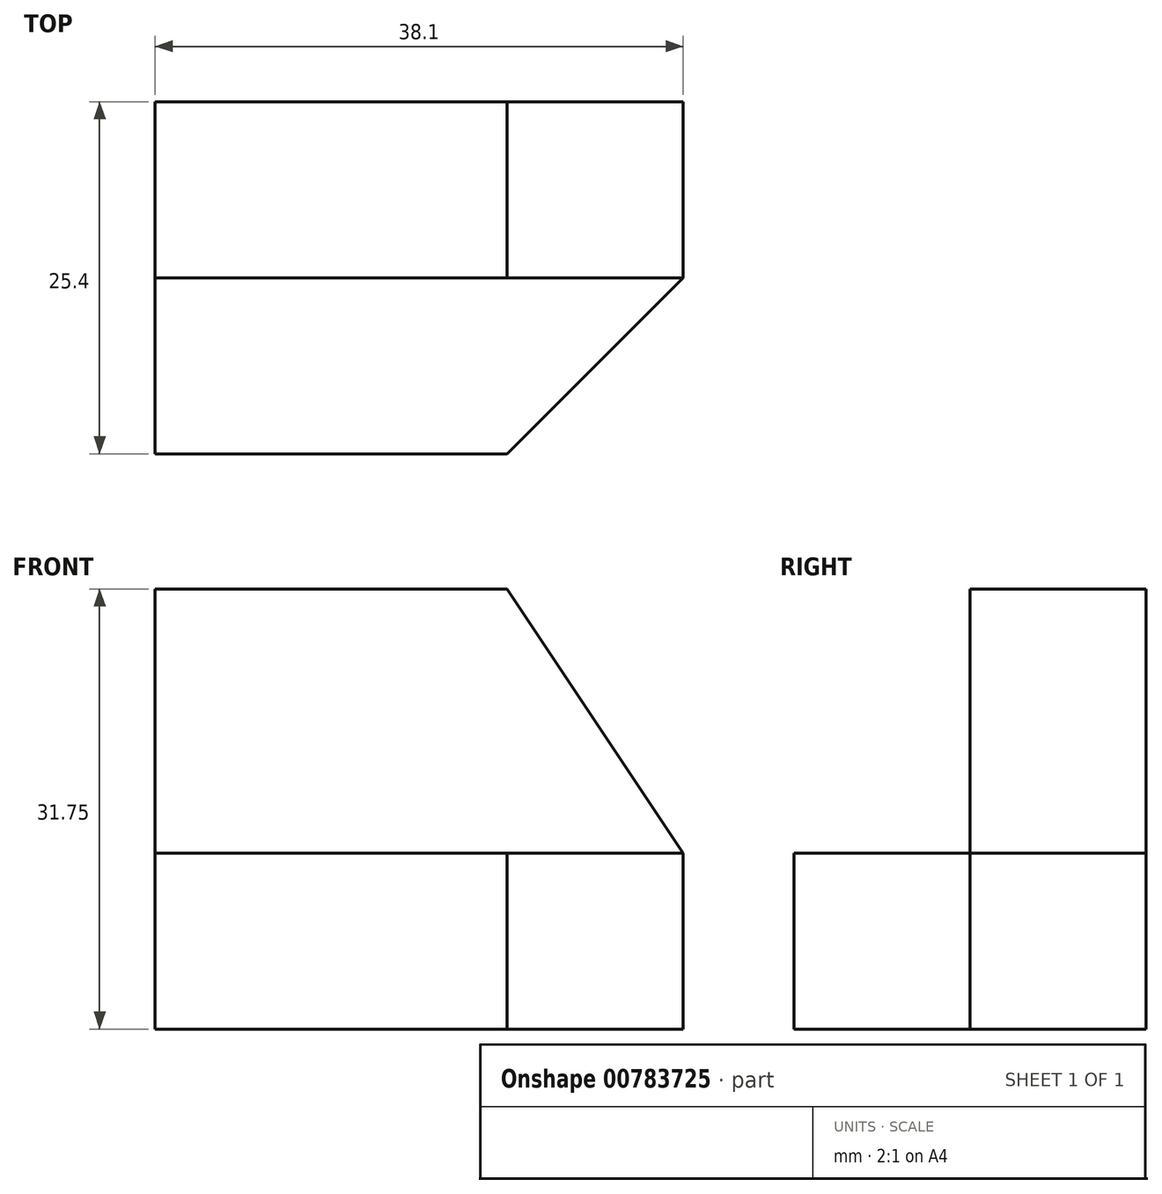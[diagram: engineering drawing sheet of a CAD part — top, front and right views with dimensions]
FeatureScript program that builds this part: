
annotation { "Feature Type Name" : "Feature", "Feature Type Description" : "" }
export const myFeature = defineFeature(function(context is Context, id is Id, definition is map)
    precondition{}
    {
        {
            var Q0;
            Q0=qCreatedBy(makeId("Front.planeOp"),FACE);
            var sketch = newSketch(context, id + "F0", { "sketchPlane" : qUnion([Q0])});
            skLineSegment(sketch, "E0", {"start": v(0, 0) * mm, "end": v(38.1, 0) * mm});
            skLineSegment(sketch, "E1", {"start": v(0, 0) * mm, "end": v(0, 31.75) * mm});
            skLineSegment(sketch, "E2", {"start": v(0, 31.75) * mm, "end": v(38.1, 31.75) * mm});
            skLineSegment(sketch, "E3", {"start": v(38.1, 31.75) * mm, "end": v(38.1, 0) * mm});
            skSolve(sketch);
        }
        {
            var Q0;
            Q0=makeQuery(id+"F0.imprint","IMPRINT",FACE,{"disambiguationData":[TD([[makeQuery(id+"F0.imprint","IMPRINT",EDGE,{"derivedFrom":sQuery(id+"F0.wireOp",EDGE,"E0")}),1.0]])]});
            extrude(context, id + "F1", {"entities" : qUnion([Q0]), "depth" : 25.4 * mm, "offsetDistance" : 25.4 * mm});
        }
        {
            var Q0;
            Q0=makeQuery(id+"F1.opExtrude","SWEPT_FACE",FACE,{"disambiguationData":[OSD([sQuery(id+"F0.wireOp",EDGE,"E3")])]});
            var sketch = newSketch(context, id + "F2", { "sketchPlane" : qUnion([Q0])});
            skLineSegment(sketch, "E4", {"start": v(0, 31.75) * mm, "end": v(-12.7, 31.75) * mm});
            skLineSegment(sketch, "E5", {"start": v(-25.4, 0) * mm, "end": v(-25.4, 12.7) * mm});
            skLineSegment(sketch, "E6", {"start": v(-25.4, 12.7) * mm, "end": v(-12.7, 12.7) * mm});
            skLineSegment(sketch, "E7", {"start": v(-12.7, 12.7) * mm, "end": v(-12.7, 31.75) * mm});
            skSolve(sketch);
        }
        {
            var Q0;
            {var subQ0=sQuery(id+"F2.wireOp",EDGE,"E6");Q0=makeQuery(id+"F2.imprint","IMPRINT",FACE,{"disambiguationData":[TD([[makeQuery(id+"F2.imprint","IMPRINT",EDGE,{"derivedFrom":subQ0}),1.0]])]});}
            extrude(context, id + "F3", {"entities" : qUnion([Q0]), "operationType" : NewBodyOperationType.REMOVE, "oppositeDirection" : true, "depth" : 38.1 * mm, "offsetDistance" : 25.4 * mm});
        }
        {
            var Q0;
            Q0=makeQuery(id+"F3.boolean.opBoolean","COPY",FACE,{"derivedFrom":makeQuery(id+"F3.opExtrude","SWEPT_FACE",FACE,{"disambiguationData":[OSD([sQuery(id+"F2.wireOp",EDGE,"E7")])]})});
            var sketch = newSketch(context, id + "F4", { "sketchPlane" : qUnion([Q0])});
            skLineSegment(sketch, "E8", {"start": v(0, 31.75) * mm, "end": v(25.4, 31.75) * mm});
            skLineSegment(sketch, "E9", {"start": v(25.4, 31.75) * mm, "end": v(38.1, 12.7) * mm});
            skSolve(sketch);
        }
        {
            var Q0;
            {var subQ0=sQuery(id+"F4.wireOp",EDGE,"E9");Q0=makeQuery(id+"F4.imprint","IMPRINT",FACE,{"disambiguationData":[TD([[makeQuery(id+"F4.imprint","IMPRINT",EDGE,{"derivedFrom":subQ0}),1.0]])]});}
            extrude(context, id + "F5", {"entities" : qUnion([Q0]), "operationType" : NewBodyOperationType.REMOVE, "oppositeDirection" : true, "depth" : 12.7 * mm, "offsetDistance" : 25.4 * mm});
        }
        {
            var Q0;
            Q0=makeQuery(id+"F3.boolean.opBoolean","COPY",FACE,{"derivedFrom":makeQuery(id+"F3.opExtrude","SWEPT_FACE",FACE,{"disambiguationData":[OSD([sQuery(id+"F2.wireOp",EDGE,"E6")])]})});
            var sketch = newSketch(context, id + "F6", { "sketchPlane" : qUnion([Q0])});
            skLineSegment(sketch, "E10", {"start": v(0, -25.4) * mm, "end": v(25.4, -25.4) * mm});
            skLineSegment(sketch, "E11", {"start": v(25.4, -25.4) * mm, "end": v(38.1, -12.7) * mm});
            skSolve(sketch);
        }
        {
            var Q0;
            {var subQ0=sQuery(id+"F6.wireOp",EDGE,"E11");Q0=makeQuery(id+"F6.imprint","IMPRINT",FACE,{"disambiguationData":[TD([[makeQuery(id+"F6.imprint","IMPRINT",EDGE,{"derivedFrom":subQ0}),-1.0]])]});}
            extrude(context, id + "F7", {"entities" : qUnion([Q0]), "operationType" : NewBodyOperationType.REMOVE, "oppositeDirection" : true, "depth" : 12.7 * mm, "offsetDistance" : 25.4 * mm});
        }
    });
